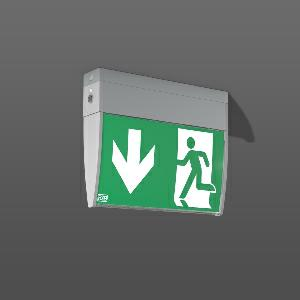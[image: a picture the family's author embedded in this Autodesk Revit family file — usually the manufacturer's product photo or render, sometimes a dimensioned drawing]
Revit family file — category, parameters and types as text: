
# Revit family: gsun_d_672219_004_1_07_ae0f
name_source: partatom
category: Lighting Fixtures
units: mm (PartAtom-declared; Revit-internal decimal feet)

## family parameters
Cut with Voids When Loaded = No
Host = Face
Light Source = No
Part Type = Normal
Room Calculation Point = No
Round Connector Dimension = Use Diameter
Shared = No

## types (1)
- GSUN D
    Apparent Load = 0 VA
    Default Elevation = 1800 mm
    Description = Series: GSUN D
Luminaire for escape route identification. Housing: extruded aluminium profile, powder-coated. 4 legends and 1 white lay in plastic sheet included. Universal mounting kit for ceiling and wall surface mounting. Electronic ballast included. Self-contained system with automatic self-test and feedback via DALI bus, only to RZB DALI monitoring system. 
Colour: silver, matt (approx. RAL 9006)
Length: 247 mm
Width: 45 mm
Height: 200 mm
Weight: 0.9 kg
Operating mode: maintained power mode
Viewing Distance: 24 m
Duration time: 3 h
Lamp: LED
Socket: without socket
Colour temperature: 4000K
System power: 4.7 W
Control gear: Regulated power supply
Protection class: I
Type of protection: IP 30
    Height = 200 mm
    Lamp = 0 x
    Length = 247 mm
    Luminous efficacy = 0 lm/W
    Manufacturer = RZB
    ModVariant = No
    Model = 672219.004.1.07
    Mounting Place = Ceiling, Wall
    Mounting Type = Surface mounted
    Number of Poles = 1
    OnlyDefault = Yes
    Power Factor = 1
    Product Name = GSUN D
    Product group = Surface mounted ceiling and wall luminaires
    ProductGroupID = 305
    Protection Class = Protection class I
    Protection Degree = IP 30
    RLX_Detail_Level = 1
    RLX_Emergency_Light_Flux = 0 lm
    RLX_Emergency_Type = 0
    RLX_Emergency_Type_DB = No
    RlxData = <blob elided: 30477 chars, md5=63880856>
    Standby Power = 0 W
    System Light Flux = 0 lm
    System Power = 0 W
    Type Comments = Product without accessories
    Type Image = 671995.004.1.jpg
    URL = http://relux.com
    VarID = ---
    Voltage = 230 V
    Voltage Range = 220-240 V
    Weight = 0.00 kg
    Width = 45 mm

## geometry (parser evidence)
native form markers: Blend x4, Sweep x10
no freeform markers — native parametric forms only
